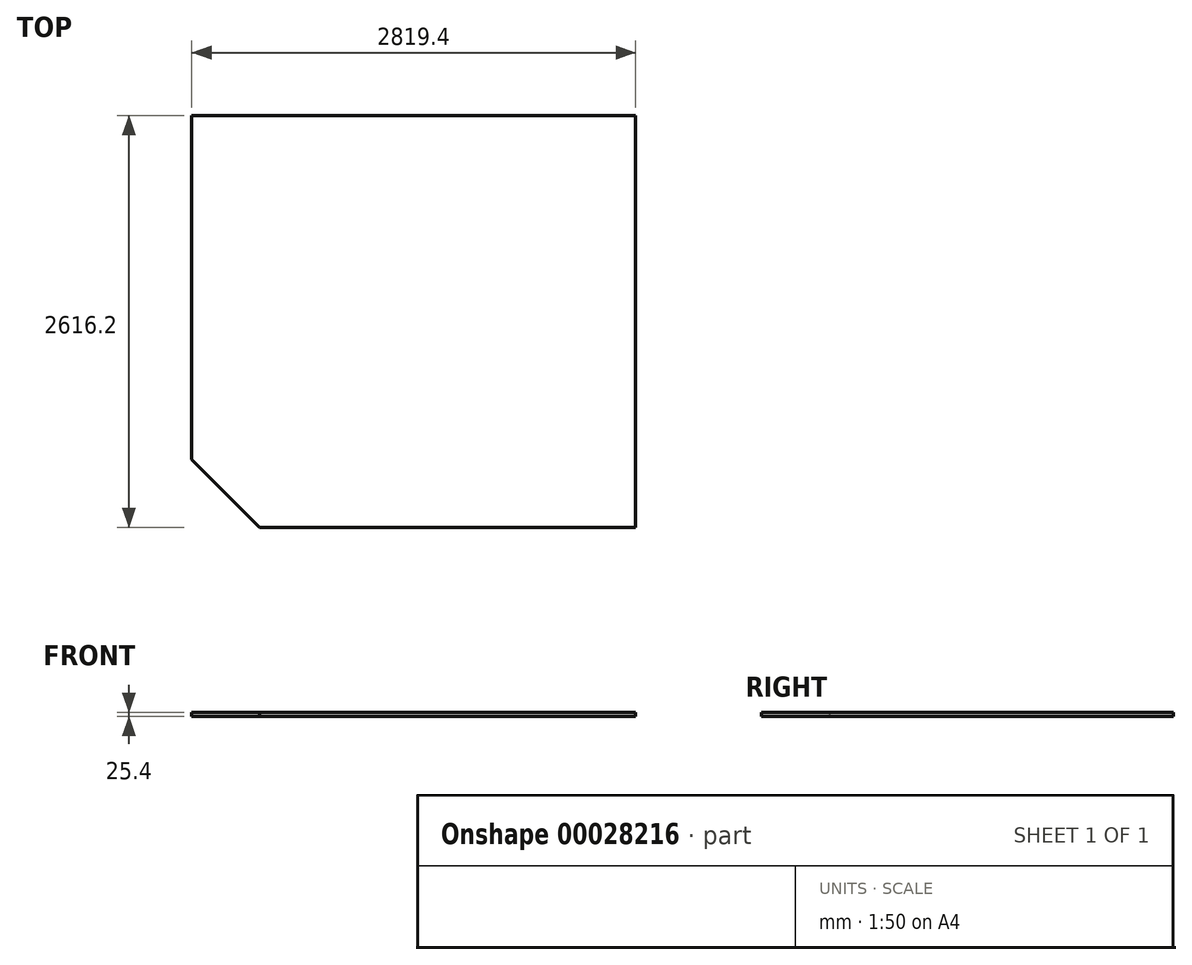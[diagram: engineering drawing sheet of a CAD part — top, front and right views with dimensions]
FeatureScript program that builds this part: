
annotation { "Feature Type Name" : "Feature", "Feature Type Description" : "" }
export const myFeature = defineFeature(function(context is Context, id is Id, definition is map)
    precondition{}
    {
        {
            var Q0;
            Q0=qCreatedBy(makeId("Top.planeOp"),FACE);
            var sketch = newSketch(context, id + "F0", { "sketchPlane" : qUnion([Q0])});
            skLineSegment(sketch, "E0.bottom", {"start": v(-6927.45, 545.26) * mm, "end": v(-4108.05, 545.26) * mm});
            skLineSegment(sketch, "E0.top", {"start": v(-6496.4, -2070.94) * mm, "end": v(-4108.05, -2070.94) * mm});
            skLineSegment(sketch, "E0.left", {"start": v(-6927.45, 545.26) * mm, "end": v(-6927.45, -1639.9) * mm});
            skLineSegment(sketch, "E1", {"start": v(-6927.45, -1639.9) * mm, "end": v(-6496.4, -2070.94) * mm});
            skLineSegment(sketch, "E2", {"start": v(-4108.05, 545.26) * mm, "end": v(-4108.05, -2070.94) * mm});
            skSolve(sketch);
        }
        {
            var Q0;
            Q0=makeQuery(id+"F0.imprint","IMPRINT",FACE,{"disambiguationData":[TD([[makeQuery(id+"F0.imprint","IMPRINT",EDGE,{"derivedFrom":sQuery(id+"F0.wireOp",EDGE,"E0.bottom")}),-1.0]])]});
            extrude(context, id + "F1", {"entities" : qUnion([Q0]), "depth" : 25.4 * mm});
        }
    });
